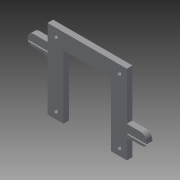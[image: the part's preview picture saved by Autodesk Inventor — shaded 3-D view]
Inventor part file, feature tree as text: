
AUTODESK INVENTOR PART (.ipt)
format: ipt  version: 2014 SP1 (Build 180222100, 222)  size: 182,272 bytes
history: native  units: mm
features: extrude x1, sketch x1
ambient origin geometry x8: Origin, YZ Plane, XZ Plane, XY Plane, X Axis, Y Axis, Z Axis, Center Point
bodies: Solid1 (feature_tree)
feature tree (2):
  extrude  "Extrusion1"  [1 undecoded]
  sketch  "Sketch1"  dims[d0=4.5mm d1=0.0mm]
note: 1 required parameter value undecoded (feature->parameter linkage not recoverable at this tier; creation-order binding heuristic only, values carry confidence <= 0.55)
